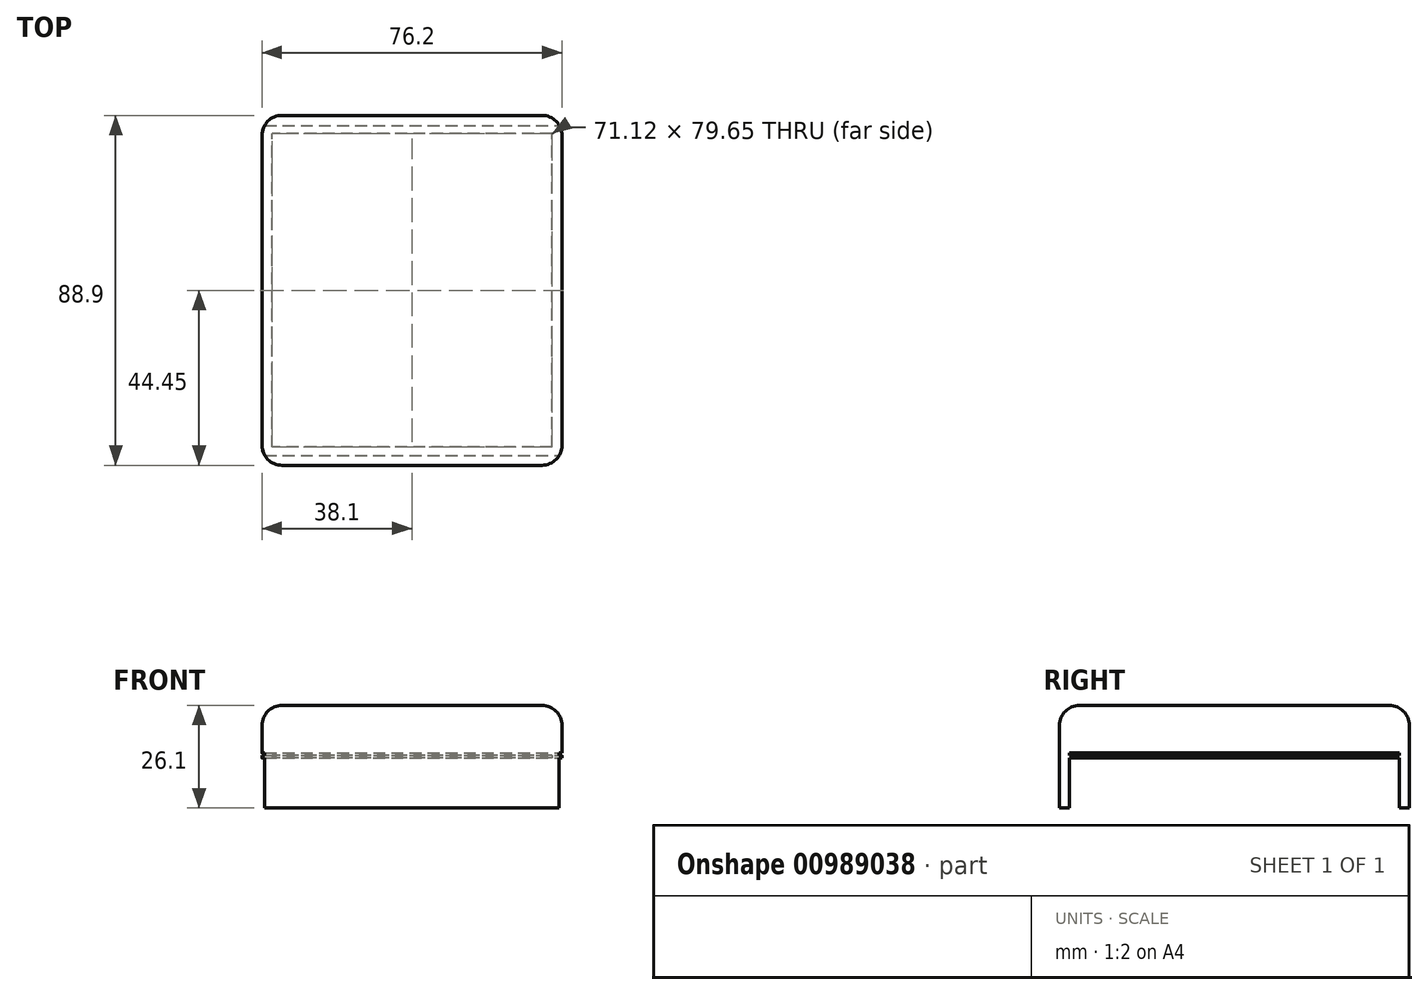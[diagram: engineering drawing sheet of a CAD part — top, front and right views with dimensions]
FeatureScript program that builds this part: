
annotation { "Feature Type Name" : "Feature", "Feature Type Description" : "" }
export const myFeature = defineFeature(function(context is Context, id is Id, definition is map)
    precondition{}
    {
        {
            var Q0;
            Q0=qCreatedBy(makeId("Right.planeOp"),FACE);
            var sketch = newSketch(context, id + "F0", { "sketchPlane" : qUnion([Q0])});
            skLineSegment(sketch, "E0", {"start": v(0, 0) * mm, "end": v(0, 26.1) * mm});
            skLineSegment(sketch, "E1", {"start": v(0, 26.1) * mm, "end": v(88.9, 26.1) * mm});
            skLineSegment(sketch, "E2", {"start": v(88.9, 26.1) * mm, "end": v(88.9, 0) * mm});
            skLineSegment(sketch, "E3", {"start": v(88.9, 0) * mm, "end": v(86.36, 0) * mm});
            skLineSegment(sketch, "E4", {"start": v(86.36, 0) * mm, "end": v(86.36, 12.7) * mm});
            skLineSegment(sketch, "E5", {"start": v(86.36, 12.7) * mm, "end": v(2.54, 12.7) * mm});
            skLineSegment(sketch, "E6", {"start": v(0, 0) * mm, "end": v(2.54, 0) * mm});
            skLineSegment(sketch, "E7", {"start": v(2.54, 0) * mm, "end": v(2.54, 12.7) * mm});
            skSolve(sketch);
        }
        {
            var Q0;
            Q0=makeQuery(id+"F0.imprint","IMPRINT",FACE,{"disambiguationData":[TD([[makeQuery(id+"F0.imprint","IMPRINT",EDGE,{"derivedFrom":sQuery(id+"F0.wireOp",EDGE,"E0")}),-1.0]])]});
            extrude(context, id + "F1", {"entities" : qUnion([Q0]), "oppositeDirection" : true, "depth" : 76.2 * mm, "offsetDistance" : 25.4 * mm});
        }
        {
            var Q0;
            Q0=makeQuery(id+"F1.opExtrude","CAP_FACE",FACE,{"disambiguationData":[OSD([sQuery(id+"F0.wireOp",EDGE,"E0"),sQuery(id+"F0.wireOp",EDGE,"E1"),sQuery(id+"F0.wireOp",EDGE,"E2"),sQuery(id+"F0.wireOp",EDGE,"E3"),sQuery(id+"F0.wireOp",EDGE,"E4"),sQuery(id+"F0.wireOp",EDGE,"E5"),sQuery(id+"F0.wireOp",EDGE,"E6"),sQuery(id+"F0.wireOp",EDGE,"E7")])],"isStart":true});
            var sketch = newSketch(context, id + "F2", { "sketchPlane" : qUnion([Q0])});
            skLineSegment(sketch, "E8.bottom", {"start": v(2.53, 13.97) * mm, "end": v(86.36, 13.97) * mm});
            skLineSegment(sketch, "E8.top", {"start": v(2.53, 13.34) * mm, "end": v(86.36, 13.34) * mm});
            skLineSegment(sketch, "E8.left", {"start": v(2.53, 13.97) * mm, "end": v(2.53, 13.34) * mm});
            skLineSegment(sketch, "E9", {"start": v(86.36, 13.97) * mm, "end": v(86.36, 13.34) * mm});
            skSolve(sketch);
        }
        {
            var Q0;
            Q0 = qSketchRegion(id + "F2", true);
            extrude(context, id + "F3", {"entities" : qUnion([Q0]), "operationType" : NewBodyOperationType.REMOVE, "endBound" : BoundingType.THROUGH_ALL, "oppositeDirection" : true, "depth" : 25.4 * mm, "offsetDistance" : 25.4 * mm});
        }
        {
            var Q0;
            Q0=makeQuery(id+"F1.opExtrude","SWEPT_FACE",FACE,{"disambiguationData":[OSD([sQuery(id+"F0.wireOp",EDGE,"E5")])]});
            var sketch = newSketch(context, id + "F4", { "sketchPlane" : qUnion([Q0])});
            skLineSegment(sketch, "E10.bottom", {"start": v(-2.54, -4.62) * mm, "end": v(-73.66, -4.62) * mm});
            skLineSegment(sketch, "E10.top", {"start": v(-2.54, -84.28) * mm, "end": v(-73.66, -84.28) * mm});
            skLineSegment(sketch, "E10.left", {"start": v(-2.54, -4.62) * mm, "end": v(-2.54, -84.28) * mm});
            skLineSegment(sketch, "E10.right", {"start": v(-73.66, -4.62) * mm, "end": v(-73.66, -84.28) * mm});
            skSolve(sketch);
        }
        {
            var Q0;
            Q0 = qSketchRegion(id + "F4", true);
            extrude(context, id + "F5", {"entities" : qUnion([Q0]), "operationType" : NewBodyOperationType.REMOVE, "oppositeDirection" : true, "depth" : 1.27 * mm, "offsetDistance" : 25.4 * mm});
        }
        {
            var Q0;
            Q0=makeQuery(id+"F1.opExtrude","SWEPT_EDGE",EDGE,{"disambiguationData":[OSD([sQuery(id+"F0.wireOp",EDGE,"E0"),sQuery(id+"F0.wireOp",EDGE,"E1")])]});
            var Q1;
            Q1=makeQuery(id+"F1.opExtrude","CAP_EDGE",EDGE,{"disambiguationData":[OSD([sQuery(id+"F0.wireOp",EDGE,"E1")])],"isStart":true});
            var Q2;
            Q2=makeQuery(id+"F1.opExtrude","SWEPT_EDGE",EDGE,{"disambiguationData":[OSD([sQuery(id+"F0.wireOp",EDGE,"E1"),sQuery(id+"F0.wireOp",EDGE,"E2")])]});
            var Q3;
            Q3=makeQuery(id+"F1.opExtrude","CAP_EDGE",EDGE,{"disambiguationData":[OSD([sQuery(id+"F0.wireOp",EDGE,"E1")])],"isStart":false});
            fillet(context, id + "F6", {"entities" : qUnion([Q0, Q1, Q2, Q3]), "radius" : 5.08 * mm, "tangentPropagation" : true, "allowEdgeOverflow" : false});
        }
        {
            var Q0;
            Q0=makeQuery(id+"F1.opExtrude","CAP_EDGE",EDGE,{"disambiguationData":[OSD([sQuery(id+"F0.wireOp",EDGE,"E0")])],"isStart":true});
            fillet(context, id + "F7", {"entities" : qUnion([Q0]), "radius" : 5.08 * mm, "tangentPropagation" : true, "allowEdgeOverflow" : false});
        }
        {
            var Q0;
            Q0=makeQuery(id+"F1.opExtrude","CAP_EDGE",EDGE,{"disambiguationData":[OSD([sQuery(id+"F0.wireOp",EDGE,"E2")])],"isStart":true});
            fillet(context, id + "F8", {"entities" : qUnion([Q0]), "radius" : 5.08 * mm, "tangentPropagation" : true, "allowEdgeOverflow" : false});
        }
        {
            var Q0;
            Q0=makeQuery(id+"F1.opExtrude","CAP_EDGE",EDGE,{"disambiguationData":[OSD([sQuery(id+"F0.wireOp",EDGE,"E0")])],"isStart":false});
            fillet(context, id + "F9", {"entities" : qUnion([Q0]), "radius" : 5.08 * mm, "tangentPropagation" : true, "allowEdgeOverflow" : false});
        }
        {
            var Q0;
            Q0=makeQuery(id+"F1.opExtrude","CAP_EDGE",EDGE,{"disambiguationData":[OSD([sQuery(id+"F0.wireOp",EDGE,"E2")])],"isStart":false});
            fillet(context, id + "F10", {"entities" : qUnion([Q0]), "radius" : 5.08 * mm, "tangentPropagation" : true, "allowEdgeOverflow" : false});
        }
    });
